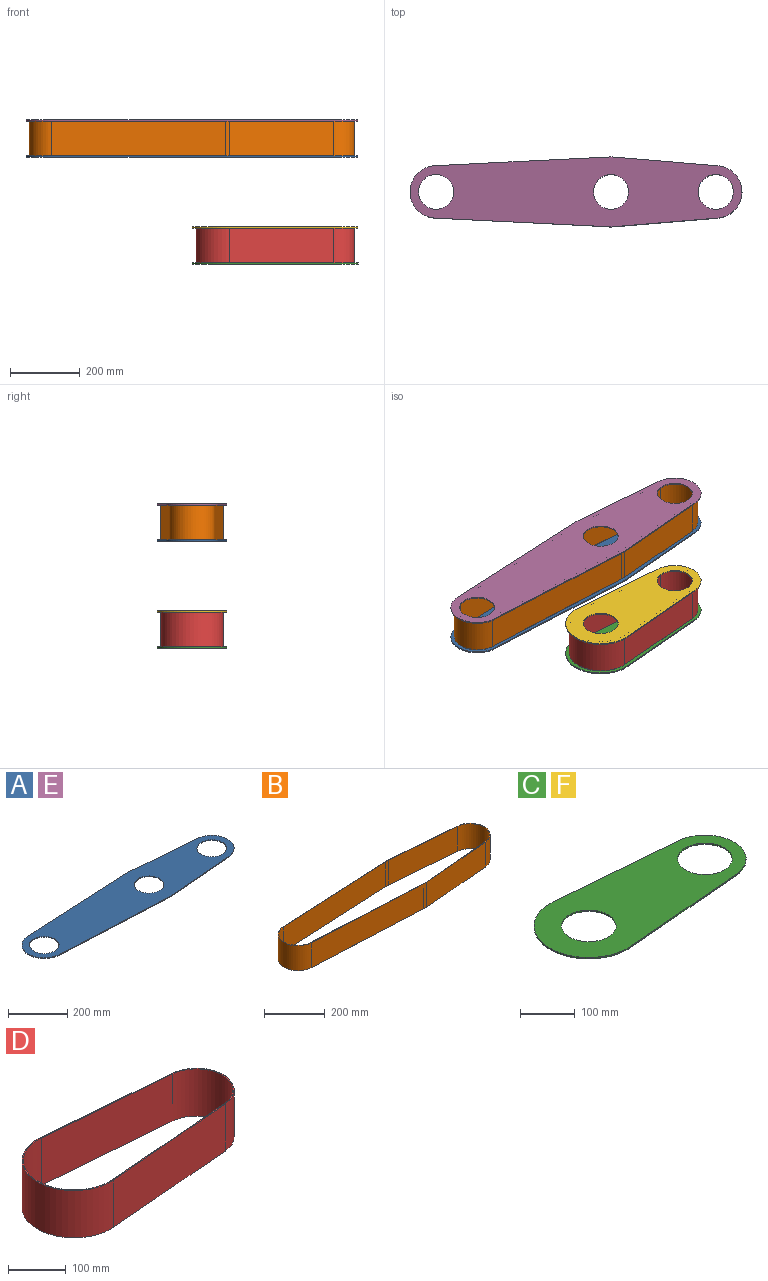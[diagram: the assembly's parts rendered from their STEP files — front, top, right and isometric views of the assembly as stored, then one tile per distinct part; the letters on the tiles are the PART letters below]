
ASSEMBLY  parts=6 mates=5
PART A: 13 faces, bbox 950x200x3 mm
  f0: plane 498.75x24.97mm, normal (-0.05,1,0), area 1498.1mm2, adj f1,f9,f11,f12
  f1: cylinder r=75mm len=149.81mm, axis (0,0,-1), area 684.3mm2, adj f0,f2,f11,f12
  f2: plane 498.75x24.97mm, normal (-0.05,-1,0), area 1498.1mm2, adj f1,f3,f11,f12
  f3: cylinder r=100mm len=13.33mm, axis (0,0,-1), area 40mm2, adj f2,f4,f11,f12
  f4: plane 297.92x24.91mm, normal (0.08,-1,0), area 896.9mm2, adj f3,f5,f11,f12
  f5: cylinder r=75mm len=149.48mm, axis (0,0,-1), area 669.3mm2, adj f4,f6,f11,f12
  f6: plane 297.92x24.91mm, normal (0.08,1,0), area 896.9mm2, adj f5,f9,f11,f12
  f7: cylinder r=50mm len=100mm, axis (0,0,-1), area 942.5mm2, adj f11,f12
  f8: cylinder r=50mm len=100mm, axis (0,0,-1), area 942.5mm2, adj f11,f12
  f9: cylinder r=100mm len=13.33mm, axis (0,0,-1), area 40mm2, adj f0,f6,f11,f12
  f10: cylinder r=50mm len=100mm, axis (0,0,-1), area 942.5mm2, adj f11,f12
  f11: plane 950x200mm, normal (0,0,1), area 134401.3mm2, adj f0,f1,f2,f3,f4,f5,f6,f7
  f12: plane 950x200mm, normal (0,0,-1), area 134401.3mm2, adj f0,f1,f2,f3,f4,f5,f6,f7
PART B: 18 faces, bbox 930x180x100 mm
  f0: plane 498.75x100mm, normal (-0.05,1,0), area 49937.5mm2, adj f1,f15,f16,f17
  f1: cylinder r=90mm len=100mm, axis (0,0,1), area 1201.1mm2, adj f0,f2,f16,f17
  f2: plane 297.92x100mm, normal (0.08,1,0), area 29895.7mm2, adj f1,f3,f16,f17
  f3: cylinder r=65mm len=129.55mm, axis (0,0,1), area 19335.8mm2, adj f2,f4,f16,f17
  f4: plane 297.92x100mm, normal (0.08,-1,0), area 29895.7mm2, adj f3,f5,f16,f17
  f5: cylinder r=90mm len=100mm, axis (0,0,1), area 1201.1mm2, adj f4,f6,f16,f17
  f6: plane 498.75x100mm, normal (-0.05,-1,0), area 49937.5mm2, adj f5,f15,f16,f17
  f7: cylinder r=88mm len=100mm, axis (0,0,1), area 1174.4mm2, adj f8,f14,f16,f17
  f8: plane 498.75x100mm, normal (0.05,-1,0), area 49937.5mm2, adj f7,f9,f16,f17
  f9: cylinder r=63mm len=125.84mm, axis (0,0,1), area 19161.8mm2, adj f8,f10,f16,f17
  f10: plane 498.75x100mm, normal (0.05,1,0), area 49937.5mm2, adj f9,f11,f16,f17
  f11: cylinder r=88mm len=100mm, axis (0,0,1), area 1174.4mm2, adj f10,f12,f16,f17
  f12: plane 297.92x100mm, normal (-0.08,1,0), area 29895.7mm2, adj f11,f13,f16,f17
  f13: cylinder r=63mm len=125.56mm, axis (0,0,1), area 18740.8mm2, adj f12,f14,f16,f17
  f14: plane 297.92x100mm, normal (-0.08,-1,0), area 29895.7mm2, adj f7,f13,f16,f17
  f15: cylinder r=65mm len=129.84mm, axis (0,0,1), area 19770.1mm2, adj f0,f6,f16,f17
  f16: plane 930x180mm, normal (0,0,-1), area 4010.9mm2, adj f0,f1,f2,f3,f4,f5,f6,f7
  f17: plane 930x180mm, normal (0,0,1), area 4010.9mm2, adj f0,f1,f2,f3,f4,f5,f6,f7
PART C: 8 faces, bbox 475x200x3 mm
  f0: cylinder r=100mm len=200mm, axis (0,0,-1), area 992.5mm2, adj f1,f5,f6,f7
  f1: plane 297.92x24.91mm, normal (0.08,-1,0), area 896.9mm2, adj f0,f2,f6,f7
  f2: cylinder r=75mm len=149.48mm, axis (0,0,-1), area 669.3mm2, adj f1,f5,f6,f7
  f3: cylinder r=50mm len=100mm, axis (0,0,-1), area 942.5mm2, adj f6,f7
  f4: cylinder r=50mm len=100mm, axis (0,0,-1), area 942.5mm2, adj f6,f7
  f5: plane 297.92x24.91mm, normal (0.08,1,0), area 896.9mm2, adj f0,f2,f6,f7
  f6: plane 475x200mm, normal (0,0,1), area 61518.1mm2, adj f0,f1,f2,f3,f4,f5
  f7: plane 475x200mm, normal (0,0,-1), area 61518.1mm2, adj f0,f1,f2,f3,f4,f5
PART D: 10 faces, bbox 455x180x100 mm
  f0: cylinder r=90mm len=180mm, axis (0,0,-1), area 29776.1mm2, adj f1,f7,f8,f9
  f1: plane 297.92x100mm, normal (0.08,-1,0), area 29895.7mm2, adj f0,f2,f8,f9
  f2: cylinder r=65mm len=129.55mm, axis (0,0,-1), area 19335.8mm2, adj f1,f7,f8,f9
  f3: plane 297.92x100mm, normal (-0.08,1,0), area 29895.7mm2, adj f4,f6,f8,f9
  f4: cylinder r=88mm len=176mm, axis (0,0,-1), area 29114.4mm2, adj f3,f5,f8,f9
  f5: plane 297.92x100mm, normal (-0.08,-1,0), area 29895.7mm2, adj f4,f6,f8,f9
  f6: cylinder r=63mm len=125.56mm, axis (0,0,-1), area 18740.8mm2, adj f3,f5,f8,f9
  f7: plane 297.92x100mm, normal (0.08,1,0), area 29895.7mm2, adj f0,f2,f8,f9
  f8: plane 455x180mm, normal (0,0,1), area 2165.5mm2, adj f0,f1,f2,f3,f4,f5,f6,f7
  f9: plane 455x180mm, normal (0,0,-1), area 2165.5mm2, adj f0,f1,f2,f3,f4,f5,f6,f7
PART E: same geometry as A
PART F: same geometry as C
PLACE A t=(624.11,-722.39,227.19)mm
PLACE B t=(624.11,-722.39,330.19)mm
PLACE C t=(624.11,-722.39,-328.81)mm
PLACE D t=(624.11,-722.39,-328.81)mm
PLACE E t=(624.11,-722.39,330.19)mm
PLACE F t=(624.11,-722.39,-225.81)mm
MATE fastened D.f4 <-> F.f0  axis (0,0,1) through (1124.11,-722.39,24.19)mm
MATE fastened C.f0 <-> D.f0  axis (0,0,1) through (1124.11,-722.39,-75.81)mm
MATE fastened F.f2 <-> A.f5  axis (0,0,1) through (1424.11,-722.39,27.19)mm
MATE fastened B.f3 <-> A.f5  axis (0,0,-1) through (1424.11,-722.39,230.19)mm
MATE fastened E.f5 <-> B.f3  axis (0,0,-1) through (1424.11,-722.39,330.19)mm
